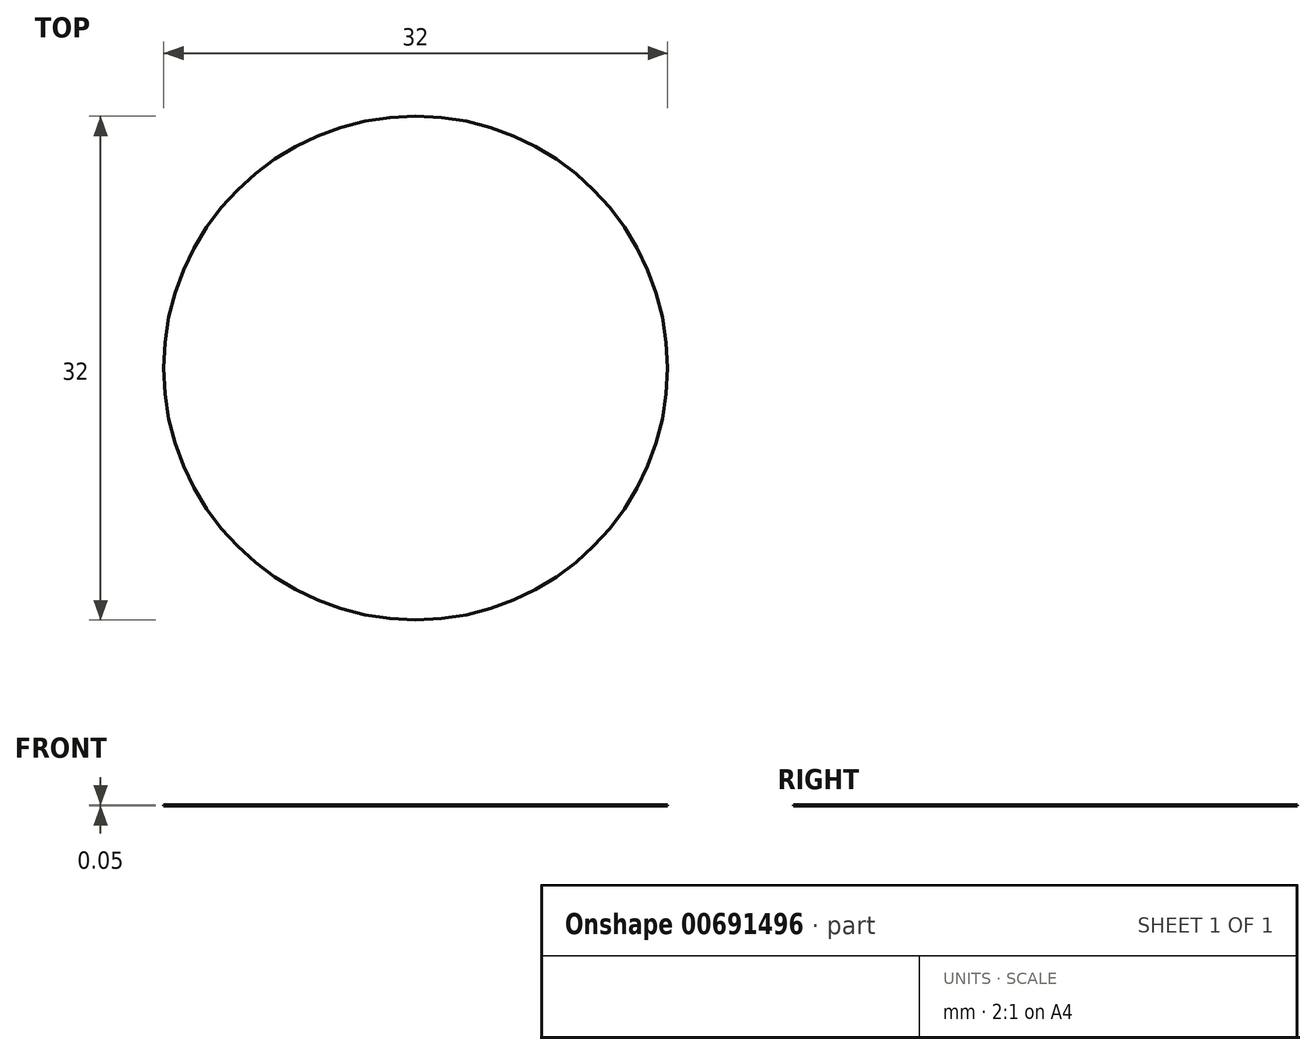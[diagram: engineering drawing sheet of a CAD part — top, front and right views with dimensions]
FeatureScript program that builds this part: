
annotation { "Feature Type Name" : "Feature", "Feature Type Description" : "" }
export const myFeature = defineFeature(function(context is Context, id is Id, definition is map)
    precondition{}
    {
        {
            var Q0;
            Q0=qCreatedBy(makeId("Top.planeOp"),FACE);
            var sketch = newSketch(context, id + "F0", { "sketchPlane" : qUnion([Q0])});
            skCircle(sketch, "E0", {"center": v(0, 0) * mm, "radius": 16 * mm});
            skSolve(sketch);
        }
        {
            var Q0;
            Q0=makeQuery(id+"F0.imprint","IMPRINT",FACE,{"disambiguationData":[TD([[makeQuery(id+"F0.imprint","IMPRINT",EDGE,{"derivedFrom":sQuery(id+"F0.wireOp",EDGE,"E0")}),1.0]])]});
            extrude(context, id + "F1", {"entities" : qUnion([Q0]), "depth" : 0.05 * mm, "offsetDistance" : 25 * mm});
        }
    });
